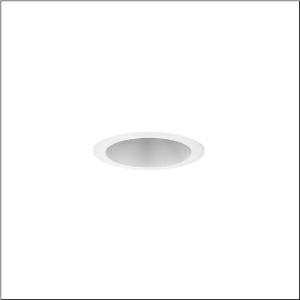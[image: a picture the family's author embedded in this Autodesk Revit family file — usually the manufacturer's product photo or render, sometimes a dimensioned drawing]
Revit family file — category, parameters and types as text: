
# Revit family: lunis_31_mini_51dn15de31
name_source: partatom
category: Lighting Fixtures
units: mm (PartAtom-declared; Revit-internal decimal feet)

## family parameters
Cut with Voids When Loaded = No
Host = Face
Light Source = No
Part Type = Normal
Room Calculation Point = No
Round Connector Dimension = Use Diameter
Shared = No

## types (1)
- Lunis 31 mini (1 x LED, 1000 lm, 8.3 W, 3000K)
    Apparent Load = 8 VA
    CIE Flux Codes = 93 98 100 100 100
    Color Rendering = 80
    Color Temperature = 3000K
    Default Elevation = 1800 mm
    Description = Lunis 31,  mini, downlight, light control with lens, light emission: direct distribution, LED rated luminous flux: 1.000lm, light colour: 830, mains connection: 220..240V, AC, 50/60Hz, housing, white, protection rating (complete): IP20, protection rating (on room side): IP54, insulation class (complete): insulation class II (safety insulation), certification: CE, packaging unit: 1 piece
    Height = 0 mm  [stored 0 ft]
    Lamp = 1 x LED
    Lamp Light Flux = 1000 lm
    Lamp Power = 8.3 W
    Lamp count = 1
    Length = 188 mm  [stored 0.616798 ft]
    Luminous efficacy = 120 lm/W
    Manufacturer = Siteco
    ModVariant = No
    Model = 51DN15DE31
    Mounting Place = Ceiling
    Mounting Type = Recessed
    Number of Poles = 1
    OnlyDefault = Yes
    Power Factor = 1
    Product Name = Lunis 31 mini
    Product group = downlight
    ProductGroupID = 400
    Protection Class = Protection class II
    Protection Degree = IP 20
    RLX_Detail_Level = 1
    RLX_Emergency_Light_Flux = 0 lm
    RLX_Emergency_Type = 0
    RLX_Emergency_Type_DB = No
    RlxData = <blob elided: 21773 chars, md5=d6addf7a>
    Socket = socket
    Standby Power = 0 W
    System Light Flux = 1000 lm
    System Power = 8 W
    Type Comments = Product without accessories
    Type Image = l_1005624.jpg
    URL = http://relux.com
    VarID = ---
    Voltage = 0 V
    Weight = 0.00 kg
    Width = 0 mm  [stored 0 ft]

note: [stored X ft] marks values corroborated as IEEE doubles in the binary element streams (Revit-internal decimal feet)

## geometry (parser evidence)
native form markers: Blend x4, Sweep x11
no freeform markers — native parametric forms only
